# Revit family: Bernhardt_Design-Credenzas-Matera-StandardHeight
name_source: partatom
category: Furniture
revit_build: Autodesk Revit 2016 (Build: 20150714_1515(x64)
units: mm (PartAtom-declared; Revit-internal decimal feet)

## family parameters
Always vertical = Yes
Cut with Voids When Loaded = No
OmniClass Number = 23.40.20.00
OmniClass Title = General Furniture and Specialties
Room Calculation Point = No
Shared = No
Work Plane-Based = No

## types (14) — shared parameters
Manufacturer = Bernhardt Design
Matera Metal = <By Category>
Matera Top = <By Category>
Matera Veneer = <By Category>
Model = Matera
Tabletop_depth = 20 5/8"
Tabletop_halfDepth = 10 5/16"
URL = http://www.bernhardtdesign.com

## per-type parameters (varying)
| type | Catalog | SKU | Tabletop_halfWidth | Tabletop_width | base_width | inside_18in-18in | inside_20in-20in-20in | inside_24in-12in | inside_24in-24in | inside_24in-24inDrawers | inside_24in-36inDrawers | leg_width | outside | outside_open | subTop_width |
| Matera - SAJ,SJJ | SAJ,SJJ | SAJ,SJJ | 48" | 96" | 42" | No | No | No | Yes | No | No | 24 3/16" | Yes | No | 47 5/32" |
| Matera - SBJ,SFJ | SBJ,SFJ | SBJ,SFJ | 48" | 96" | 42" | No | No | No | Yes | No | No | 24 3/16" | No | Yes | 47 5/32" |
| Matera - SHH | SHH | SHH | 54" | 108" | 48" | No | No | No | No | No | Yes | 30 3/16" | Yes | No | 53 5/32" |
| Matera - SLJ,SKJ | SLJ,SKJ | SLJ,SKJ | 48" | 96" | 42" | No | No | No | No | Yes | No | 24 3/16" | Yes | No | 47 5/32" |
| Matera - SAN | SAN | SAN | 36" | 72" | 30" | Yes | No | No | No | No | No | 18 3/16" | Yes | No | 35 5/32" |
| Matera - SFN,SEN | SFN,SEN | SFN,SEN | 36" | 72" | 30" | No | No | Yes | No | No | No | 18 3/16" | Yes | No | 35 5/32" |
| Matera - SBN | SBN | SBN | 36" | 72" | 30" | Yes | No | No | No | No | No | 18 3/16" | No | Yes | 35 5/32" |
| Matera - SDN | SDN | SDN | 36" | 72" | 30" | No | No | Yes | No | No | No | 18 3/16" | No | Yes | 35 5/32" |
| Matera - SAL,SJL | SAL,SJL | SAL,SJL | 42" | 84" | 36" | No | No | No | Yes | No | No | 24 3/16" | Yes | No | 41 5/32" |
| Matera - SBL,SFL | SBL,SFL | SBL,SFL | 42" | 84" | 36" | No | No | No | Yes | No | No | 24 3/16" | No | Yes | 41 5/32" |
| Matera - SCL,SGL | SCL,SGL | SCL,SGL | 42" | 84" | 36" | No | No | No | Yes | No | No | 24 3/16" | No | Yes | 41 5/32" |
| Matera - SAH,SIH | SAH,SIH | SAH,SIH | 54" | 108" | 48" | No | Yes | No | No | No | No | 30 3/16" | Yes | No | 53 5/32" |
| Matera - SBH,SFH | SBH,SFH | SBH,SFH | 54" | 108" | 48" | No | Yes | No | No | No | No | 30 3/16" | No | Yes | 53 5/32" |
| Matera - SDH | SDH | SDH | 54" | 108" | 48" | No | No | No | No | No | Yes | 30 3/16" | No | Yes | 53 5/32" |

## geometry (parser evidence)
native form markers: Sweep x2
no freeform markers — native parametric forms only
